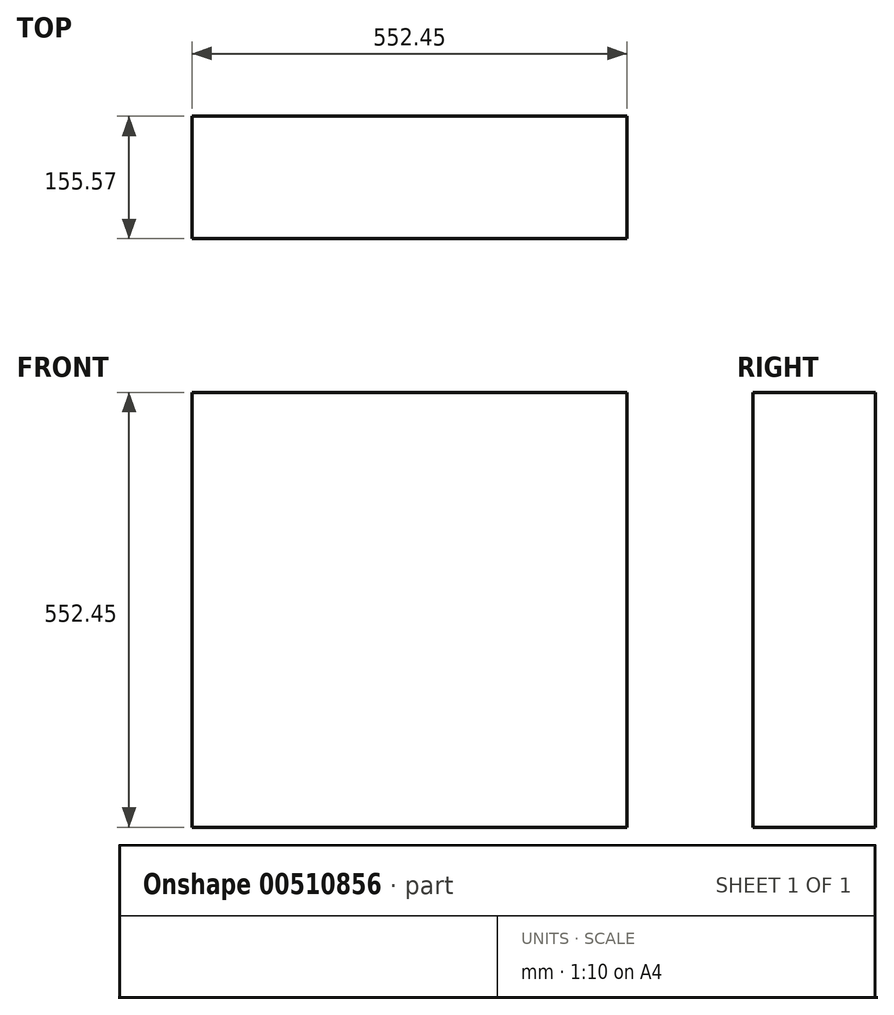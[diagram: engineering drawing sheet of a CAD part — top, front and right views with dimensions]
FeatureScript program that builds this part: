
annotation { "Feature Type Name" : "Feature", "Feature Type Description" : "" }
export const myFeature = defineFeature(function(context is Context, id is Id, definition is map)
    precondition{}
    {
        {
            var Q0;
            Q0=qCreatedBy(makeId("Front.planeOp"),FACE);
            var sketch = newSketch(context, id + "F0", { "sketchPlane" : qUnion([Q0])});
            skLineSegment(sketch, "E0.bottom", {"start": v(-271.94, 301.08) * mm, "end": v(280.51, 301.08) * mm});
            skLineSegment(sketch, "E0.top", {"start": v(-271.94, -251.37) * mm, "end": v(280.51, -251.37) * mm});
            skLineSegment(sketch, "E0.left", {"start": v(-271.94, 301.08) * mm, "end": v(-271.94, -251.37) * mm});
            skLineSegment(sketch, "E0.right", {"start": v(280.51, 301.08) * mm, "end": v(280.51, -251.37) * mm});
            skSolve(sketch);
        }
        {
            var Q0;
            Q0=makeQuery(id+"F0.imprint","IMPRINT",FACE,{"disambiguationData":[TD([[makeQuery(id+"F0.imprint","IMPRINT",EDGE,{"derivedFrom":sQuery(id+"F0.wireOp",EDGE,"E0.bottom")}),-1.0]])]});
            extrude(context, id + "F1", {"entities" : qUnion([Q0]), "depth" : 155.57 * mm});
        }
    });
